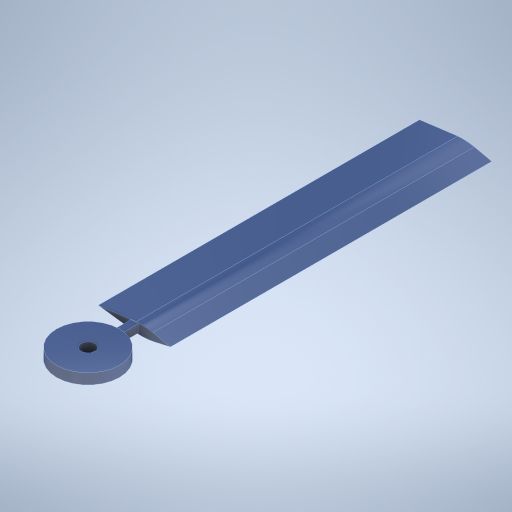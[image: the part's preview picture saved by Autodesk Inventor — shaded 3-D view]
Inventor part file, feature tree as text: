
AUTODESK INVENTOR PART (.ipt)
format: ipt  version: 2023 (Build 270158000, 158)  size: 285,696 bytes
history: native  units: mm
features: extrude x4, sketch x4, mirror x1, plane x1
ambient origin geometry x8: Origin, YZ Plane, XZ Plane, XY Plane, X Axis, Y Axis, Z Axis, Center Point
bodies: Solid1 (feature_tree)
feature tree (10):
  extrude  "Extrusion1"  Depth=55.0mm
  mirror  "Mirror1"
  extrude  "Extrusion2"  Depth=245.0mm TaperAngle=0.0deg
  plane  "Work Plane1"
  extrude  "Extrusion3"  Depth=3.7mm
  extrude  "Extrusion4"  Depth=5.492mm
  sketch  "Sketch1"  dims[d0=55.0mm d1=35.0mm]
  sketch  "Sketch2"  dims[d2=4.5mm d3=245.0mm d4=0.0mm]
  sketch  "Sketch3"  dims[d5=27.5mm d6=3.7mm]
  sketch  "Sketch4"  dims[d7=2.5mm d8=27.5mm d9=3.0mm d10=10.0mm d11=0.0mm d12=-3.1mm d13=5.492mm d14=25.5mm d15=48.0mm d16=10.5mm d17=4.0mm d18=4.0mm d19=0.0mm d20=0.0mm d21=15.0mm d22=0.0mm d23=0.5mm d24=0.872665mm]
